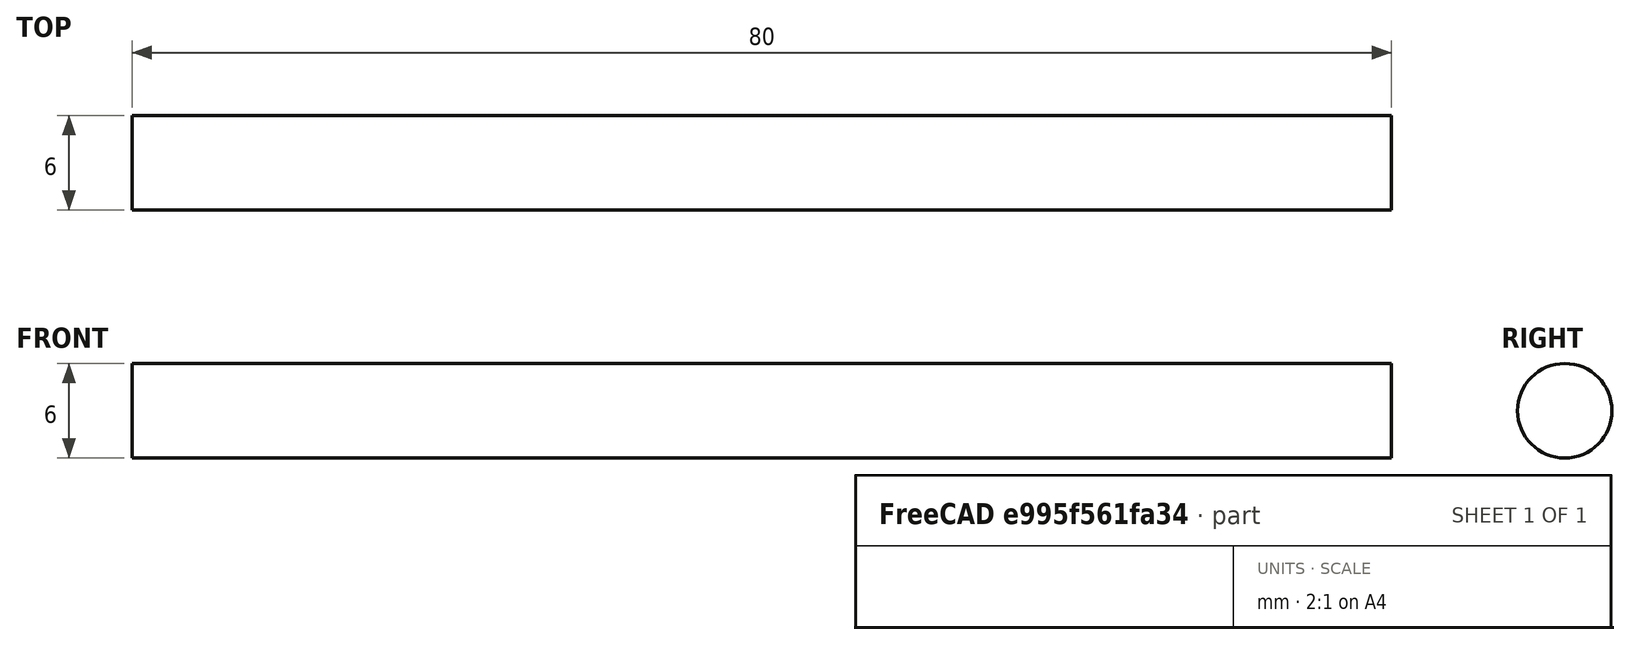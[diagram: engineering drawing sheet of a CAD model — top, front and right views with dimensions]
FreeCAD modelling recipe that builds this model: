
FCSTD DOCUMENT  (FreeCAD 0.18R15441 (Git))
Label: Rod_M6x80mm
License: All rights reserved
LicenseURL: http://en.wikipedia.org/wiki/All_rights_reserved
objects: Sketcher::SketchObject×1, PartDesign::Pad×1, PartDesign::Body×1, App::Part×1
note: 4 computed .brp shape members not serialized (recipe doc carries the construction recipe); baked Part::Feature solids carry a one-line shape summary decoded from their .brp

FEATURE [Sketcher::SketchObject] Sketch  label="RodSketch"
  MapMode = 5
  Placement = pos=(0,0,0) rot=(0.57735,0.57735,0.57735;2.0944rad)
  Support = -> [YZ_Plane001]
  sketch-geometry (1):
    g0: Circle CenterX=0 CenterY=0 CenterZ=0 NormalX=0 NormalY=0 NormalZ=1 AngleXU=0 Radius=3
  constraints (2):
    c: Coincident(g0,g-1)
    c: Radius(g0) = 3
FEATURE [PartDesign::Pad] Pad  label="RodPad"
  Length = 80
  Length2 = 100
  Midplane = true
  Placement = pos=(0,0,0) rot=(0.57735,0.57735,0.57735;2.0944rad)
  Profile = -> Sketch
  Type = 0
FEATURE [PartDesign::Body] Body  label="RodBody"
  Group = -> [Sketch,Pad]
  Origin = -> Origin001
  Tip = -> Pad
FEATURE [App::Part] Part  label="Rod_M6x80_Part"
  Group = -> [Body]
  License = CC BY 3.0
  LicenseURL = http://creativecommons.org/licenses/by/3.0/
  Origin = -> Origin
